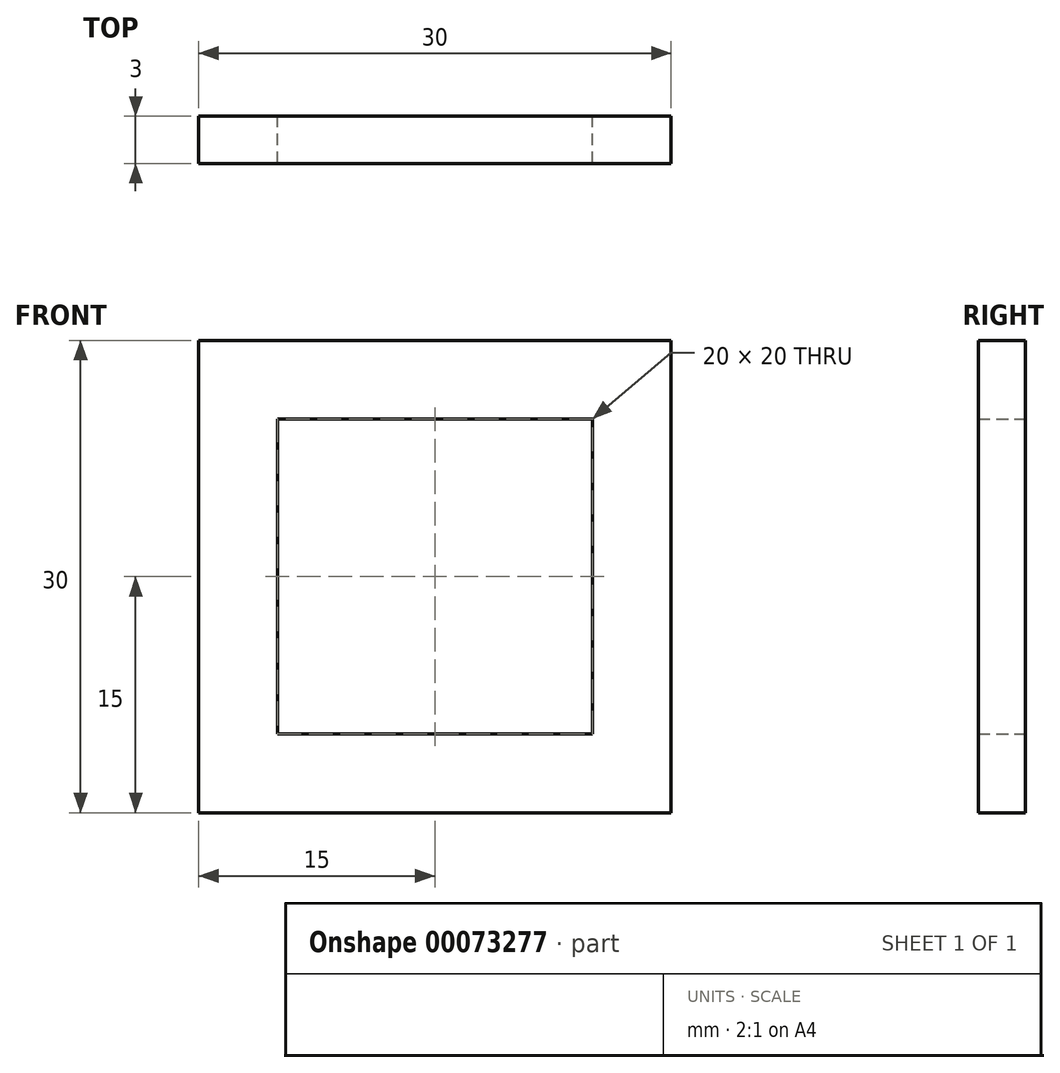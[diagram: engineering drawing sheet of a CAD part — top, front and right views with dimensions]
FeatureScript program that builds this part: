
annotation { "Feature Type Name" : "Feature", "Feature Type Description" : "" }
export const myFeature = defineFeature(function(context is Context, id is Id, definition is map)
    precondition{}
    {
        {
            var Q0;
            Q0=qCreatedBy(makeId("Front.planeOp"),FACE);
            var sketch = newSketch(context, id + "F0", { "sketchPlane" : qUnion([Q0])});
            skLineSegment(sketch, "E0.rect.bottom", {"start": v(15, -15) * mm, "end": v(-15, -15) * mm});
            skLineSegment(sketch, "E0.rect.top", {"start": v(15, 15) * mm, "end": v(-15, 15) * mm});
            skLineSegment(sketch, "E0.rect.left", {"start": v(15, -15) * mm, "end": v(15, 15) * mm});
            skLineSegment(sketch, "E0.rect.right", {"start": v(-15, -15) * mm, "end": v(-15, 15) * mm});
            skPoint(sketch, "E0.rect.middle", {"position": v(0, 0) * mm});
            skLineSegment(sketch, "E1.rect.bottom", {"start": v(10, -10) * mm, "end": v(-10, -10) * mm});
            skLineSegment(sketch, "E1.rect.top", {"start": v(10, 10) * mm, "end": v(-10, 10) * mm});
            skLineSegment(sketch, "E1.rect.left", {"start": v(10, -10) * mm, "end": v(10, 10) * mm});
            skLineSegment(sketch, "E1.rect.right", {"start": v(-10, -10) * mm, "end": v(-10, 10) * mm});
            skSolve(sketch);
        }
        {
            var Q0;
            Q0 = qSketchRegion(id + "F0", true);
            extrude(context, id + "F1", {"entities" : qUnion([Q0]), "depth" : 3 * mm});
        }
    });
